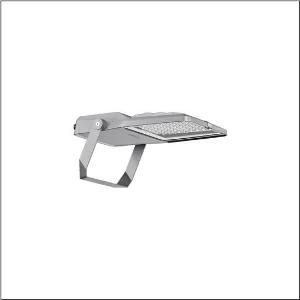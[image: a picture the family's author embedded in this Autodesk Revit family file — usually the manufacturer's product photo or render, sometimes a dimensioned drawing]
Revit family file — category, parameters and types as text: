
# Revit family: floodlight_fl_21_iq_mini___pl43_5xa7772b2a1a_654d
name_source: partatom
category: Lighting Fixtures
units: mm (PartAtom-declared; Revit-internal decimal feet)

## family parameters
Cut with Voids When Loaded = No
Host = Face
Light Source = No
Part Type = Normal
Room Calculation Point = No
Round Connector Dimension = Use Diameter
Shared = No

## types (1)
- --- (1 x LED, 6400 lm, 45.5 W, 3000K)
    Apparent Load = 46 VA
    CIE Flux Codes = 27 78 99 100 100
    Color Rendering = 70
    Color Temperature = 3000K
    Default Elevation = 1800 mm
    Description = Floodlight FL 21 iQ mini, floodlight, primary light control with lens, of PMMA, primary optical cover: protective disc, of toughened safety glass, transparent, light distribution: PL43, light emission: direct distribution, installation type: surface-mounted, LED, High Power LED, rated luminous flux: 6.400lm, luminous efficacy: 141lm/W, light colour: 730, colour temperature: 3000K, control: Street-Remote, Auto-Match, Temp-Guard, Night-Set, Smart-Wire, Desk-Remote (wireless, voltage-free reading and setting of iQ features in the workshop via application-optimized NFC function/RFID function), optimised constant luminous flux control (CLO 2.0), with terminal, 6-pole, mains connection: 220..240V, AC, 50/60Hz, start of lifetime: 46W, end of service life: 48W, reduction: 22W, luminaire housing, of diecast aluminium, powder-coated, Siteco® metallic grey (DB 702S), corrosivity category C5 mid according to DIN EN ISO 12944, sealing non-destructively replaceable, mounting bracket, of steel, galvanised, powder-coated, Siteco® metallic grey (DB 702S), protection rating (complete): IP66, insulation class (complete): insulation class II (safety insulation), certification: CE, ENEC, VDE, protection symbol: D, impact resistance: IK08, permissible operating ambient temperature: -40..+40°C, permissible operating ambient temperature for outdoor applications: -40..+50°C, standard: DIN EN 12944, LABS conformity tested according to VDMA 24364:2018-05, packaging unit: 1 piece

Light Distribution: PL43
    Height = 70 mm
    Lamp = 1 x LED
    Lamp Light Flux = 6400 lm
    Lamp Power = 45.5 W
    Lamp count = 1
    Length = 485 mm
    Luminous efficacy = 141 lm/W
    Manufacturer = Siteco
    ModVariant = No
    Model = 5XA7772B2A1A
    Number of Poles = 1
    OnlyDefault = Yes
    Power Factor = 1
    Product Name = Floodlight FL 21 iQ mini | PL43
    Product group = floodlight | pylon annexe
    ProductGroupID = 6200
    Protection Class = Protection class II
    Protection Degree = IP 66
    RLX_Detail_Level = 1
    RLX_Emergency_Light_Flux = 0 lm
    RLX_Emergency_Type = 0
    RLX_Emergency_Type_DB = No
    RlxData = <blob elided: 95973 chars, md5=bb8c9b21>
    Socket = socket
    Standby Power = 0 W
    System Light Flux = 6400 lm
    System Power = 46 W
    Type Comments = factory setting: luminous flux: 100 % | dim-lin: 254 | 463 mA
    Type Image = l_1006845.jpg
    URL = http://relux.com
    VarID = @adj_113121
    Voltage = 0 V
    Weight = 0.00 kg
    Width = 337 mm

## geometry (parser evidence)
native form markers: Blend x4, Sweep x12
no freeform markers — native parametric forms only
